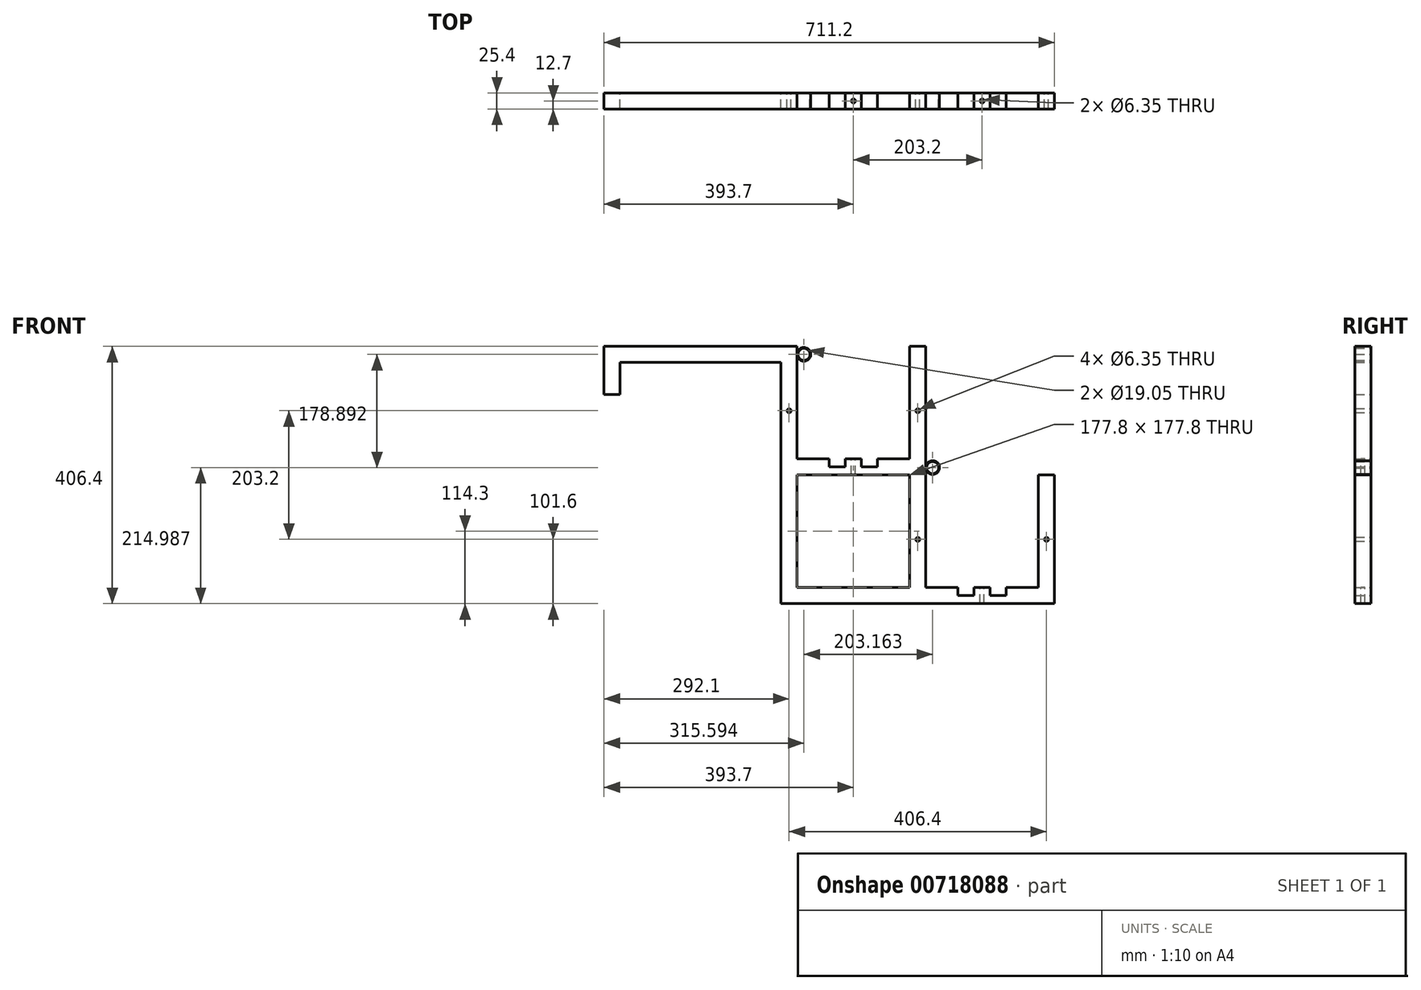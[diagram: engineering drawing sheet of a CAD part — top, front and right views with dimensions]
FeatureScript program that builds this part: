
annotation { "Feature Type Name" : "Feature", "Feature Type Description" : "" }
export const myFeature = defineFeature(function(context is Context, id is Id, definition is map)
    precondition{}
    {
        {
            var Q0;
            Q0=qCreatedBy(makeId("Front.planeOp"),FACE);
            var sketch = newSketch(context, id + "F0", { "sketchPlane" : qUnion([Q0])});
            skLineSegment(sketch, "E0.bottom", {"start": v(127, -12.7) * mm, "end": v(-127, -12.7) * mm});
            skLineSegment(sketch, "E0.top", {"start": v(127, 12.7) * mm, "end": v(-127, 12.7) * mm});
            skLineSegment(sketch, "E0.left", {"start": v(127, -12.7) * mm, "end": v(127, 12.7) * mm});
            skLineSegment(sketch, "E0.right", {"start": v(-127, -12.7) * mm, "end": v(-127, 12.7) * mm});
            skPoint(sketch, "E0.middle", {"position": v(0, 0) * mm});
            skLineSegment(sketch, "E1.bottom", {"start": v(-127, 12.7) * mm, "end": v(-152.4, 12.7) * mm});
            skLineSegment(sketch, "E1.top", {"start": v(-127, -63.5) * mm, "end": v(-152.4, -63.5) * mm});
            skLineSegment(sketch, "E1.left", {"start": v(-127, 12.7) * mm, "end": v(-127, -63.5) * mm});
            skLineSegment(sketch, "E1.right", {"start": v(-152.4, 12.7) * mm, "end": v(-152.4, -63.5) * mm});
            skLineSegment(sketch, "E2.bottom", {"start": v(127, 12.7) * mm, "end": v(152.4, 12.7) * mm});
            skLineSegment(sketch, "E2.top", {"start": v(127, -393.7) * mm, "end": v(152.4, -393.7) * mm});
            skLineSegment(sketch, "E2.left", {"start": v(127, 12.7) * mm, "end": v(127, -393.7) * mm});
            skLineSegment(sketch, "E2.right", {"start": v(152.4, 12.7) * mm, "end": v(152.4, -393.7) * mm});
            skLineSegment(sketch, "E3.bottom", {"start": v(152.4, -393.7) * mm, "end": v(533.4, -393.7) * mm});
            skLineSegment(sketch, "E3.top", {"start": v(152.4, -368.3) * mm, "end": v(406.4, -368.3) * mm});
            skLineSegment(sketch, "E3.left", {"start": v(152.4, -393.7) * mm, "end": v(152.4, -368.3) * mm});
            skLineSegment(sketch, "E3.right", {"start": v(533.4, -393.7) * mm, "end": v(533.4, -368.3) * mm});
            skLineSegment(sketch, "E4.bottom", {"start": v(533.4, -393.7) * mm, "end": v(558.8, -393.7) * mm});
            skLineSegment(sketch, "E4.top", {"start": v(533.4, -190.5) * mm, "end": v(558.8, -190.5) * mm});
            skLineSegment(sketch, "E4.left", {"start": v(533.4, -393.7) * mm, "end": v(533.4, -190.5) * mm});
            skLineSegment(sketch, "E4.right", {"start": v(558.8, -393.7) * mm, "end": v(558.8, -190.5) * mm});
            skLineSegment(sketch, "E5.bottom", {"start": v(330.2, -368.3) * mm, "end": v(355.6, -368.3) * mm});
            skLineSegment(sketch, "E5.top", {"start": v(330.2, 12.7) * mm, "end": v(355.6, 12.7) * mm});
            skLineSegment(sketch, "E5.left", {"start": v(330.2, -368.3) * mm, "end": v(330.2, 12.7) * mm});
            skLineSegment(sketch, "E5.right", {"start": v(355.6, -368.3) * mm, "end": v(355.6, 12.7) * mm});
            skLineSegment(sketch, "E6.bottom", {"start": v(152.4, -190.5) * mm, "end": v(330.2, -190.5) * mm});
            skLineSegment(sketch, "E6.top", {"start": v(152.4, -165.1) * mm, "end": v(203.2, -165.1) * mm});
            skLineSegment(sketch, "E6.left", {"start": v(152.4, -190.5) * mm, "end": v(152.4, -165.1) * mm});
            skLineSegment(sketch, "E6.right", {"start": v(330.2, -190.5) * mm, "end": v(330.2, -165.1) * mm});
            skLineSegment(sketch, "E7.top", {"start": v(203.2, -177.8) * mm, "end": v(228.6, -177.8) * mm});
            skLineSegment(sketch, "E7.left", {"start": v(203.2, -165.1) * mm, "end": v(203.2, -177.8) * mm});
            skLineSegment(sketch, "E7.right", {"start": v(228.6, -165.1) * mm, "end": v(228.6, -177.8) * mm});
            skLineSegment(sketch, "E8.trimOffspring", {"start": v(228.6, -165.1) * mm, "end": v(254, -165.1) * mm});
            skLineSegment(sketch, "E9.top", {"start": v(279.4, -177.8) * mm, "end": v(254, -177.8) * mm});
            skLineSegment(sketch, "E9.left", {"start": v(279.4, -165.1) * mm, "end": v(279.4, -177.8) * mm});
            skLineSegment(sketch, "E9.right", {"start": v(254, -165.1) * mm, "end": v(254, -177.8) * mm});
            skLineSegment(sketch, "E10.trimOffspring", {"start": v(279.4, -165.1) * mm, "end": v(330.2, -165.1) * mm});
            skLineSegment(sketch, "E11.top", {"start": v(406.4, -381) * mm, "end": v(431.8, -381) * mm});
            skLineSegment(sketch, "E11.left", {"start": v(406.4, -368.3) * mm, "end": v(406.4, -381) * mm});
            skLineSegment(sketch, "E11.right", {"start": v(431.8, -368.3) * mm, "end": v(431.8, -381) * mm});
            skLineSegment(sketch, "E12.trimOffspring", {"start": v(431.8, -368.3) * mm, "end": v(457.2, -368.3) * mm});
            skLineSegment(sketch, "E13.top", {"start": v(482.6, -381) * mm, "end": v(457.2, -381) * mm});
            skLineSegment(sketch, "E13.left", {"start": v(482.6, -368.3) * mm, "end": v(482.6, -381) * mm});
            skLineSegment(sketch, "E13.right", {"start": v(457.2, -368.3) * mm, "end": v(457.2, -381) * mm});
            skLineSegment(sketch, "E14.trimOffspring", {"start": v(482.6, -368.3) * mm, "end": v(533.4, -368.3) * mm});
            skCircle(sketch, "E15", {"center": v(546.1, -292.1) * mm, "radius": 3.18 * mm});
            skPoint(sketch, "E15.centerSnap0", {"position": v(546.1, -190.5) * mm});
            skCircle(sketch, "E16", {"center": v(342.9, -88.9) * mm, "radius": 3.17 * mm});
            skPoint(sketch, "E16.centerSnap0", {"position": v(342.9, 12.7) * mm});
            skCircle(sketch, "E17", {"center": v(342.9, -292.1) * mm, "radius": 3.17 * mm});
            skPoint(sketch, "E17.centerSnap0", {"position": v(342.9, -368.3) * mm});
            skCircle(sketch, "E18", {"center": v(139.7, -88.9) * mm, "radius": 3.17 * mm});
            skPoint(sketch, "E18.centerSnap0", {"position": v(139.7, 12.7) * mm});
            skCircle(sketch, "E19", {"center": v(163.2, 0.18) * mm, "radius": 10.8 * mm});
            skPoint(sketch, "E19.first.point", {"position": v(152.4, 0) * mm});
            skPoint(sketch, "E19.second.point", {"position": v(173.99, 0) * mm});
            skPoint(sketch, "E19.third.point", {"position": v(165.1, 10.8) * mm});
            skCircle(sketch, "E20", {"center": v(163.2, 0.18) * mm, "radius": 9.53 * mm});
            skCircle(sketch, "E21", {"center": v(366.36, -178.71) * mm, "radius": 10.8 * mm});
            skPoint(sketch, "E21.first.point", {"position": v(355.6, -177.8) * mm});
            skPoint(sketch, "E21.second.point", {"position": v(377.11, -177.8) * mm});
            skPoint(sketch, "E21.second.point.positionSnap0", {"position": v(355.6, -177.8) * mm});
            skPoint(sketch, "E21.third.point", {"position": v(367.16, -167.95) * mm});
            skCircle(sketch, "E22", {"center": v(366.36, -178.71) * mm, "radius": 9.52 * mm});
            skSolve(sketch);
        }
        {
            var Q0;
            {var subQ1=makeQuery(id+"F0.imprint","IMPRINT",EDGE,{"derivedFrom":sQuery(id+"F0.wireOp",EDGE,"E3.right")});var subQ2=sQuery(id+"F0.wireOp",EDGE,"E5.right");var subQ8=sQuery(id+"F0.wireOp",EDGE,"E3.bottom");var subQ9=sQuery(id+"F0.wireOp",EDGE,"E2.right");var subQ13=sQuery(id+"F0.wireOp",EDGE,"E21");var subQ14=makeQuery(id+"F0.imprint","INTERSECT",VERTEX,{"disambiguationData":[OD(0.0)],"derivedFrom":[subQ2,subQ13]});var subQ16=makeQuery(id+"F0.imprint","IMPRINT",EDGE,{"disambiguationData":[TD([[subQ14,1.0]])],"derivedFrom":subQ2});var subQ17=sQuery(id+"F0.wireOp",EDGE,"E19");var subQ18=makeQuery(id+"F0.imprint","INTERSECT",VERTEX,{"disambiguationData":[OD(0.0)],"derivedFrom":[subQ9,subQ17]});var subQ20=makeQuery(id+"F0.imprint","IMPRINT",EDGE,{"disambiguationData":[TD([[subQ18,1.0]])],"derivedFrom":subQ9});var subQ22=makeQuery(id+"F0.imprint","IMPRINT",EDGE,{"derivedFrom":sQuery(id+"F0.wireOp",EDGE,"E0.left")});var subQ23=makeQuery(id+"F0.imprint","IMPRINT",EDGE,{"derivedFrom":sQuery(id+"F0.wireOp",EDGE,"E0.right")});var subQ27=sQuery(id+"F0.wireOp",EDGE,"E6.bottom");var subQ31=sQuery(id+"F0.wireOp",EDGE,"E5.top");Q0=qUnion([makeQuery(id+"F0.imprint","IMPRINT",FACE,{"disambiguationData":[TD([[subQ20,-1.0]])]}),makeQuery(id+"F0.imprint","IMPRINT",FACE,{"disambiguationData":[TD([[makeQuery(id+"F0.imprint","IMPRINT",EDGE,{"derivedFrom":subQ27}),1.0]])]}),makeQuery(id+"F0.imprint","IMPRINT",FACE,{"disambiguationData":[TD([[makeQuery(id+"F0.imprint","IMPRINT",EDGE,{"derivedFrom":subQ31}),-1.0]])]}),makeQuery(id+"F0.imprint","IMPRINT",FACE,{"disambiguationData":[TD([[subQ1,-1.0]])]}),makeQuery(id+"F0.imprint","IMPRINT",FACE,{"disambiguationData":[TD([[subQ23,1.0]])]}),makeQuery(id+"F0.imprint","IMPRINT",FACE,{"disambiguationData":[TD([[subQ22,-1.0]])]}),makeQuery(id+"F0.imprint","IMPRINT",FACE,{"disambiguationData":[TD([[makeQuery(id+"F0.imprint","IMPRINT",EDGE,{"derivedFrom":sQuery(id+"F0.wireOp",EDGE,"E0.bottom")}),-1.0]])]}),makeQuery(id+"F0.imprint","IMPRINT",FACE,{"disambiguationData":[TD([[subQ16,1.0]])]}),makeQuery(id+"F0.imprint","IMPRINT",FACE,{"disambiguationData":[TD([[makeQuery(id+"F0.imprint","IMPRINT",EDGE,{"derivedFrom":sQuery(id+"F0.wireOp",EDGE,"E20")}),-1.0]])]}),makeQuery(id+"F0.imprint","IMPRINT",FACE,{"disambiguationData":[TD([[makeQuery(id+"F0.imprint","IMPRINT",EDGE,{"derivedFrom":sQuery(id+"F0.wireOp",EDGE,"E22")}),-1.0]])]}),makeQuery(id+"F0.imprint","IMPRINT",FACE,{"disambiguationData":[TD([[makeQuery(id+"F0.imprint","IMPRINT",EDGE,{"derivedFrom":subQ8}),1.0]])]})]);}
            extrude(context, id + "F1", {"entities" : qUnion([Q0]), "depth" : 25.4 * mm, "offsetDistance" : 25.4 * mm});
        }
        {
            var Q0;
            Q0=makeQuery(id+"F1.opExtrude","SWEPT_FACE",FACE,{"disambiguationData":[OSD([sQuery(id+"F0.wireOp",EDGE,"E8.trimOffspring")])]});
            var sketch = newSketch(context, id + "F2", { "sketchPlane" : qUnion([Q0])});
            skCircle(sketch, "E23", {"center": v(241.3, -12.7) * mm, "radius": 3.17 * mm});
            skPoint(sketch, "E23.centerSnap0", {"position": v(228.6, -12.7) * mm});
            skPoint(sketch, "E23.centerSnap1", {"position": v(241.3, -25.4) * mm});
            skSolve(sketch);
        }
        {
            var Q0;
            Q0 = qSketchRegion(id + "F2", true);
            extrude(context, id + "F3", {"entities" : qUnion([Q0]), "operationType" : NewBodyOperationType.REMOVE, "oppositeDirection" : true, "depth" : 25.4 * mm, "offsetDistance" : 25.4 * mm});
        }
        {
            var Q0;
            Q0=makeQuery(id+"F1.opExtrude","SWEPT_FACE",FACE,{"disambiguationData":[OSD([sQuery(id+"F0.wireOp",EDGE,"E12.trimOffspring")])]});
            var sketch = newSketch(context, id + "F4", { "sketchPlane" : qUnion([Q0])});
            skCircle(sketch, "E24", {"center": v(444.5, -12.7) * mm, "radius": 3.18 * mm});
            skPoint(sketch, "E24.centerSnap0", {"position": v(431.8, -12.7) * mm});
            skPoint(sketch, "E24.centerSnap1", {"position": v(444.5, -25.4) * mm});
            skSolve(sketch);
        }
        {
            var Q0;
            Q0 = qSketchRegion(id + "F4", true);
            extrude(context, id + "F5", {"entities" : qUnion([Q0]), "operationType" : NewBodyOperationType.REMOVE, "oppositeDirection" : true, "depth" : 25.4 * mm, "offsetDistance" : 25.4 * mm});
        }
    });
